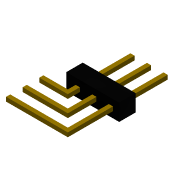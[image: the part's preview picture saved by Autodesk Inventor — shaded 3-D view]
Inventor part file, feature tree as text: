
AUTODESK INVENTOR PART (.ipt)
format: ipt  version: 2015 (Build 190159000, 159)  size: 141,312 bytes
history: native  units: in
note: dims shown in document units (in); Inventor stores cm internally (conversion verified against a paired STEP export)
features: projected_geometry x4, extrude x2, sketch x2
ambient origin geometry x8: Origin, YZ Plane, XZ Plane, XY Plane, X Axis, Y Axis, Z Axis, Center Point
bodies: Solid1 (feature_tree)
feature tree (8):
  extrude  "Extrusion1"  Depth=0.1in
  extrude  "Extrusion3"  Depth=0.1in
  sketch  "Sketch1"  dims[d14=0.025in d15=0.0in d24=0.1in]
  sketch  "Sketch3"  dims[d25=0.1in d26=0.1in d27=0.1in d29=0.025in d30=0.23in d32=0.1in d33=0.32in d34=0.09in d35=0.07in d36=0.06in d37=0.1in d38=0.32in d39=0.0575in d40=0.0375in d41=0.1in d42=0.0in d44=0.1in d45=0.19in]
  projected_geometry  "Projected Loop4"
  projected_geometry  "Projected Loop5"
  projected_geometry  "Projected Loop6"
  projected_geometry  "Projected Loop7"
